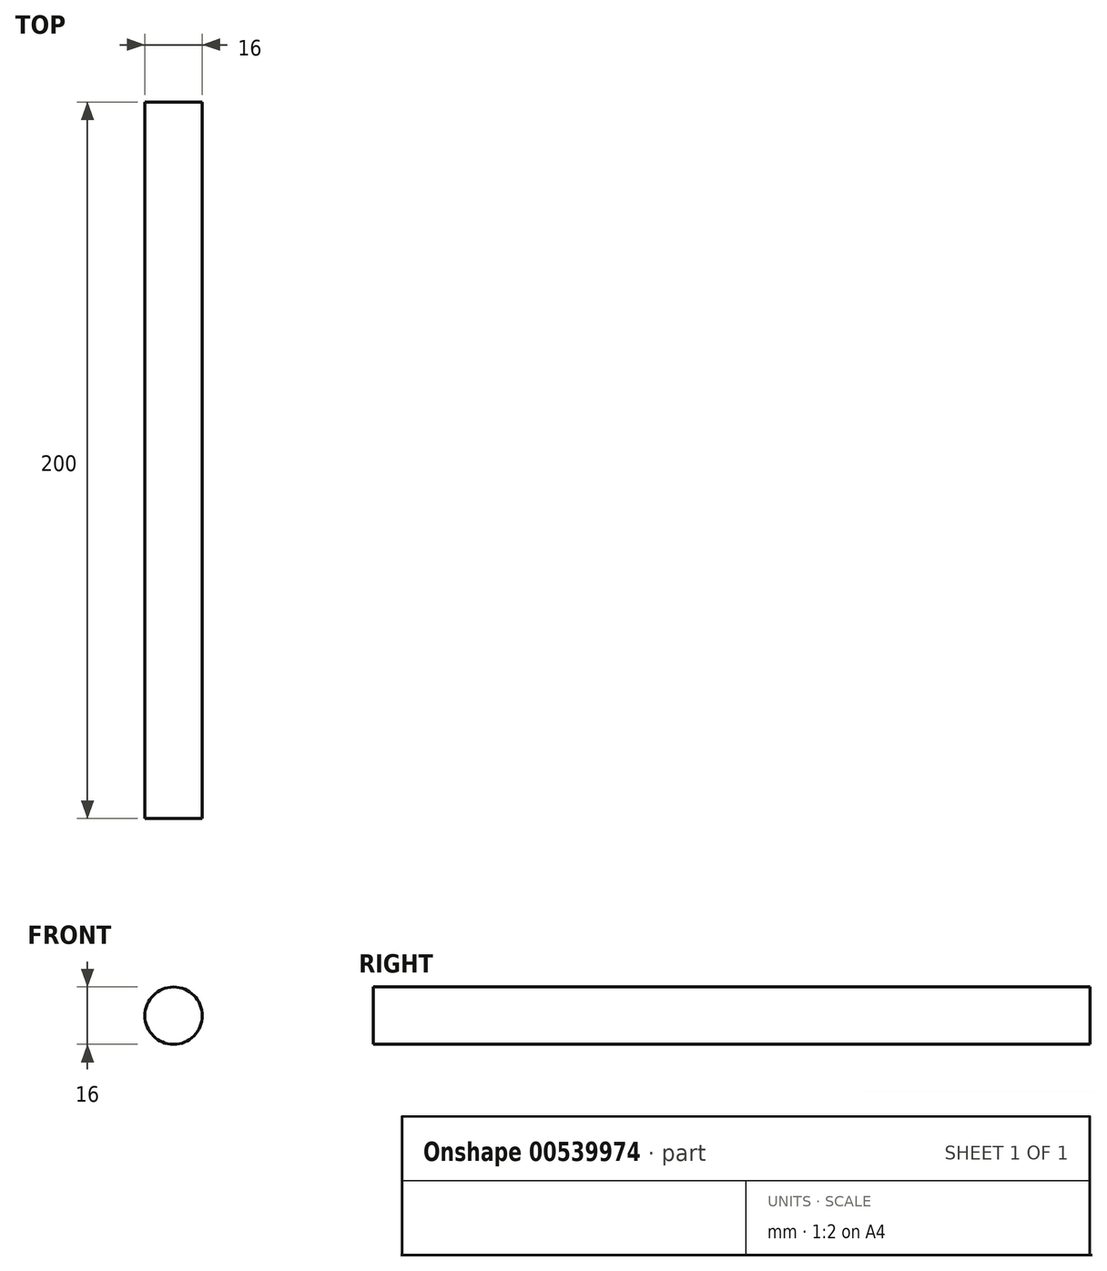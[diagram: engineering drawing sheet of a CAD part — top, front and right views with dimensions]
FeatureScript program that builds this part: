
annotation { "Feature Type Name" : "Feature", "Feature Type Description" : "" }
export const myFeature = defineFeature(function(context is Context, id is Id, definition is map)
    precondition{}
    {
        {
            var Q0;
            Q0=qCreatedBy(makeId("Front.planeOp"),FACE);
            var sketch = newSketch(context, id + "F0", { "sketchPlane" : qUnion([Q0])});
            skCircle(sketch, "E0", {"center": v(0, 0) * mm, "radius": 8 * mm});
            skSolve(sketch);
        }
        {
            var Q0;
            Q0=makeQuery(id+"F0.imprint","IMPRINT",FACE,{"disambiguationData":[TD([[makeQuery(id+"F0.imprint","IMPRINT",EDGE,{"derivedFrom":sQuery(id+"F0.wireOp",EDGE,"E0")}),1.0]])]});
            extrude(context, id + "F1", {"entities" : qUnion([Q0]), "depth" : 200 * mm, "offsetDistance" : 25 * mm});
        }
    });
